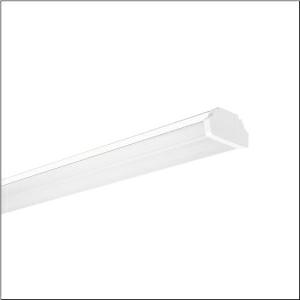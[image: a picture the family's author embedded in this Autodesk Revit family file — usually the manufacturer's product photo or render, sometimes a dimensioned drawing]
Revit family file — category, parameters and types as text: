
# Revit family: dus_31_gen_2_53bd812cv6a5d2_532a
name_source: partatom
category: Lighting Fixtures
units: mm (PartAtom-declared; Revit-internal decimal feet)

## family parameters
Cut with Voids When Loaded = No
Host = Face
Light Source = No
Part Type = Normal
Room Calculation Point = No
Round Connector Dimension = Use Diameter
Shared = No

## types (1)
- --- (1 x LED, 10550 lm, 56.5 W, 6500K)
    Apparent Load = 57 VA
    CIE Flux Codes = 47 80 95 93 100
    Color Rendering = 80
    Color Temperature = 6500K
    Default Elevation = 1800 mm
    Description = DUS 31 Gen.2, luminaire insert, of sheet steel, coil coated, white, length: 1.535mm, width: 81mm, height: 90mm, 5x system unit, system units: 307mm, LED rated luminous flux: 10.550lm, light colour: 865, SDCM (Standard Deviation of Colour Matching)MacAdam ≤ 3 SDCM (initial), control gear: ON/OFF Multilumen, CLOi, with plug, 3-pole, with phase selection, mains connection: 220..240V, AC, 50/60Hz, start of lifetime: 57W, end of service life: 68W, through-wiring accessed according to module size, primary optical cover: cover, of PMMA, light emission: direct distribution, primary light characteristic: symmetric, protection rating (complete): IP20, protection rating (LED compartment): IP50, insulation class (complete): insulation class I (protective earthing), certification: CE, ENEC, VDE, UKCA, impact resistance: IK03, permissible ambient temperature for indoor applications: -35..+40°C, corresponds to IFS (International Featured Standards) requirements for safety and quality in the food industry, reducing of maximum allowable ambient temperature of 5°C with ceiling mounting, packaging unit: 1 piece
    Height = 95 mm
    Lamp = 1 x LED
    Lamp Light Flux = 10550 lm
    Lamp Power = 56.5 W
    Lamp count = 1
    Length = 1535 mm
    Luminous efficacy = 187 lm/W
    Manufacturer = Siteco
    ModVariant = No
    Model = 53BD812CV6A5D2
    Mounting Place = Ceiling
    Mounting Type = Pendant
    Number of Poles = 1
    OnlyDefault = Yes
    Power Factor = 1
    Product Name = DUS 31 Gen.2
    Product group = luminaire insert | ceiling pendant
    ProductGroupID = 901
    Protection Class = Protection class I
    Protection Degree = IP 20
    RLX_Detail_Level = 1
    RLX_Emergency_Light_Flux = 0 lm
    RLX_Emergency_Type = 0
    RLX_Emergency_Type_DB = No
    RlxData = <blob elided: 29829 chars, md5=3fd03e99>
    Socket = socket
    Standby Power = 0 W
    System Light Flux = 10550 lm
    System Power = 57 W
    Type Comments = factory setting: luminous flux: 100 % | (A | C | E) | 133 mA
    Type Image = l_1319596.jpg
    URL = http://relux.com
    VarID = @adj_042333
    Voltage = 0 V
    Weight = 0.00 kg
    Width = 81 mm

## geometry (parser evidence)
native form markers: Blend x4, Sweep x13
no freeform markers — native parametric forms only
